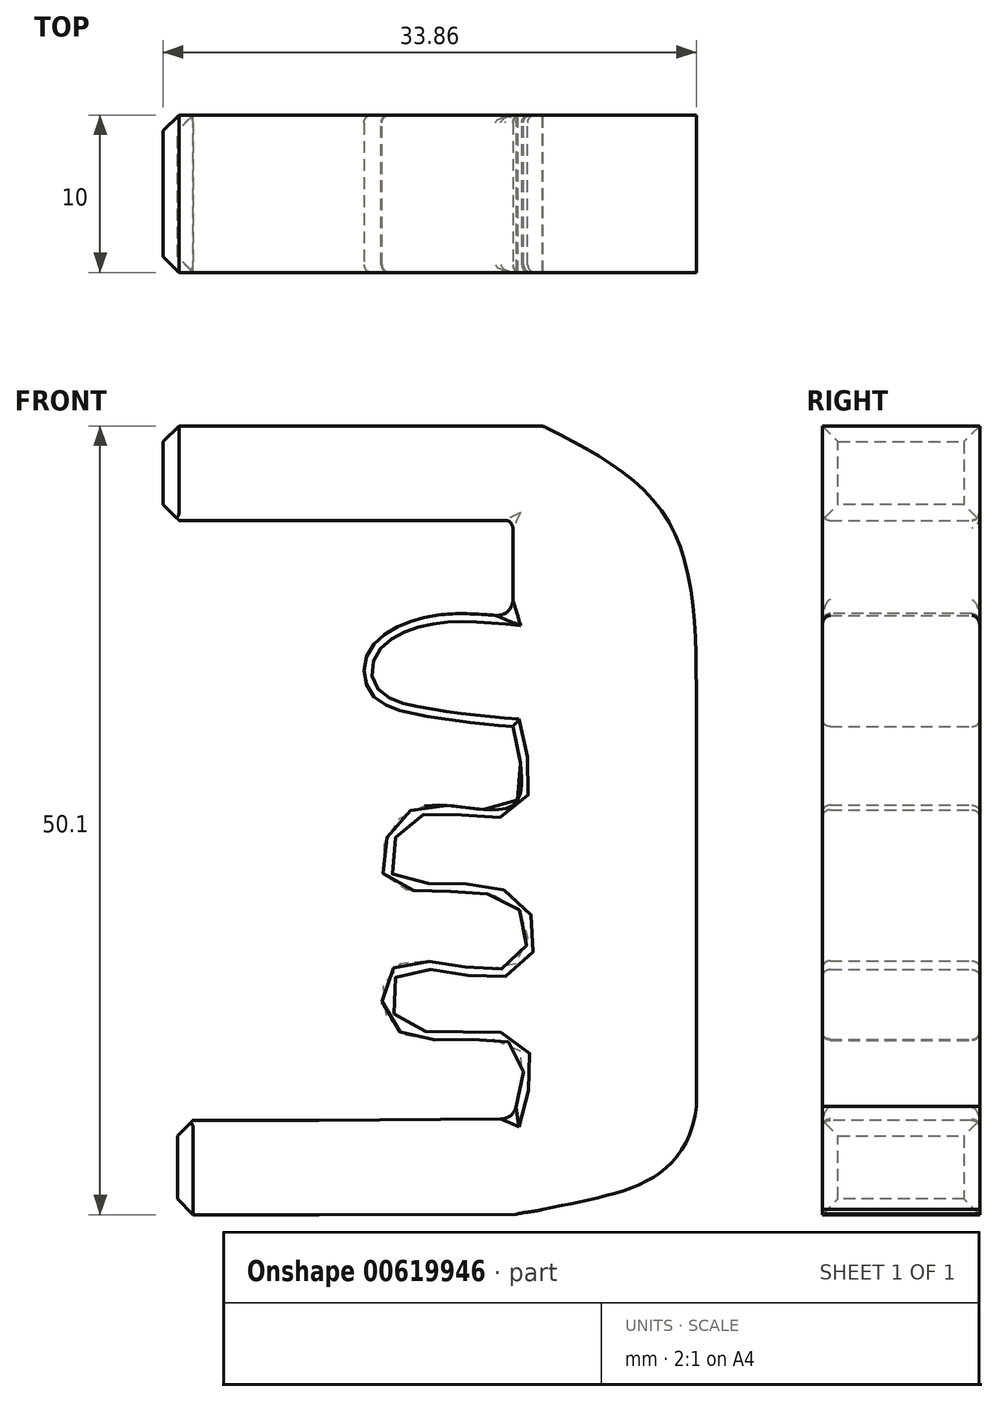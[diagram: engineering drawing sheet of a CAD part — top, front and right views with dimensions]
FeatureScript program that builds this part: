
annotation { "Feature Type Name" : "Feature", "Feature Type Description" : "" }
export const myFeature = defineFeature(function(context is Context, id is Id, definition is map)
    precondition{}
    {
        {
            var Q0;
            Q0=qCreatedBy(makeId("Front.planeOp"),FACE);
            var sketch = newSketch(context, id + "F0", { "sketchPlane" : qUnion([Q0])});
            skLineSegment(sketch, "E0.bottom", {"start": v(-57.75, 36.74) * mm, "end": v(-48.75, 36.74) * mm});
            skLineSegment(sketch, "E0.top", {"start": v(-57.75, 30.74) * mm, "end": v(-48.75, 30.74) * mm});
            skLineSegment(sketch, "E0.left", {"start": v(-57.75, 36.74) * mm, "end": v(-57.75, 30.74) * mm});
            skLineSegment(sketch, "E0.right", {"start": v(-48.75, 36.74) * mm, "end": v(-48.75, 30.74) * mm});
            skLineSegment(sketch, "E1.bottom", {"start": v(-56.85, -7.36) * mm, "end": v(-47.85, -7.36) * mm});
            skLineSegment(sketch, "E1.top", {"start": v(-56.85, -13.36) * mm, "end": v(-47.85, -13.36) * mm});
            skLineSegment(sketch, "E1.left", {"start": v(-56.85, -7.36) * mm, "end": v(-56.85, -13.36) * mm});
            skLineSegment(sketch, "E1.right", {"start": v(-47.85, -7.36) * mm, "end": v(-47.85, -13.36) * mm});
            skFitSpline(sketch, "E2", {"points": [v(-48.75, 36.74) * mm, v(-33.64, 36.74) * mm], "startDerivative": vector(17.1, 0) * mm, "endDerivative": vector(17.1, 0) * mm});
            skFitSpline(sketch, "E3", {"points": [v(-33.64, 36.74) * mm, v(-25.7, 30.74) * mm, v(-23.9, 19.03) * mm], "startDerivative": vector(20.1, -10.1) * mm, "endDerivative": vector(-0.03, -25.1) * mm});
            skFitSpline(sketch, "E4", {"points": [v(-23.9, 19.03) * mm, v(-23.89, 3) * mm], "startDerivative": vector(0, -15.9) * mm, "endDerivative": vector(0, -15.9) * mm});
            skFitSpline(sketch, "E5", {"points": [v(-23.89, 3) * mm, v(-23.89, -6.48) * mm], "startDerivative": vector(0, -10.8) * mm, "endDerivative": vector(0, -10.8) * mm});
            skFitSpline(sketch, "E6", {"points": [v(-23.89, -6.48) * mm, v(-33.64, -13.03) * mm], "startDerivative": vector(-1.93, -15.73) * mm, "endDerivative": vector(-13.6, -2.99) * mm});
            skFitSpline(sketch, "E7", {"points": [v(-48.75, 30.74) * mm, v(-35.54, 30.74) * mm], "startDerivative": vector(13.5, 0) * mm, "endDerivative": vector(13.5, 0) * mm});
            skFitSpline(sketch, "E8", {"points": [v(-35.54, 30.74) * mm, v(-35.54, 24.6) * mm], "startDerivative": vector(0, -6) * mm, "endDerivative": vector(0, -6) * mm});
            skFitSpline(sketch, "E9", {"points": [v(-35.54, 24.6) * mm, v(-41.04, 24.6) * mm, v(-44.7, 22.4) * mm, v(-44.45, 19.63) * mm, v(-40.66, 18.25) * mm, v(-35.54, 17.64) * mm], "startDerivative": vector(-25.8, 2.5) * mm, "endDerivative": vector(24.5, -1.76) * mm});
            skFitSpline(sketch, "E10", {"points": [v(-35.54, 17.64) * mm, v(-35.54, 12.64) * mm, v(-40.66, 12.64) * mm, v(-43.43, 10.86) * mm, v(-43.25, 7.65) * mm, v(-35.54, 6.4) * mm, v(-35.54, 2.48) * mm, v(-42.9, 2.48) * mm, v(-42.9, -1.63) * mm, v(-35.54, -2.52) * mm, v(-35.54, -7.28) * mm], "startDerivative": vector(15.19, -66.55) * mm, "endDerivative": vector(-18.85, -66.96) * mm});
            skLineSegment(sketch, "E11", {"start": v(-35.54, -7.28) * mm, "end": v(-47.85, -7.36) * mm});
            skFitSpline(sketch, "E12", {"points": [v(-33.64, -13.03) * mm, v(-35.28, -13.33) * mm], "startDerivative": vector(-1.5, -0.46) * mm, "endDerivative": vector(-1.5, -0.46) * mm});
            skLineSegment(sketch, "E13", {"start": v(-35.28, -13.33) * mm, "end": v(-47.85, -13.36) * mm});
            skSolve(sketch);
        }
        {
            var Q0;
            Q0 = qSketchRegion(id + "F0", true);
            extrude(context, id + "F1", {"entities" : qUnion([Q0]), "depth" : 10 * mm, "offsetDistance" : 25 * mm});
        }
        {
            var Q0;
            Q0=makeQuery(id+"F1.opExtrude","CAP_EDGE",EDGE,{"disambiguationData":[OSD([sQuery(id+"F0.wireOp",EDGE,"E0.left")])],"isStart":false});
            var Q1;
            Q1=makeQuery(id+"F1.opExtrude","CAP_EDGE",EDGE,{"disambiguationData":[OSD([sQuery(id+"F0.wireOp",EDGE,"E0.left")])],"isStart":true});
            var Q2;
            Q2=makeQuery(id+"F1.opExtrude","CAP_EDGE",EDGE,{"disambiguationData":[OSD([sQuery(id+"F0.wireOp",EDGE,"E1.left")])],"isStart":true});
            var Q3;
            Q3=makeQuery(id+"F1.opExtrude","CAP_EDGE",EDGE,{"disambiguationData":[OSD([sQuery(id+"F0.wireOp",EDGE,"E1.left")])],"isStart":false});
            var Q4;
            Q4=makeQuery(id+"F1.opExtrude","SWEPT_EDGE",EDGE,{"disambiguationData":[OSD([sQuery(id+"F0.wireOp",EDGE,"E0.bottom"),sQuery(id+"F0.wireOp",EDGE,"E0.left")])]});
            var Q5;
            Q5=makeQuery(id+"F1.opExtrude","SWEPT_EDGE",EDGE,{"disambiguationData":[OSD([sQuery(id+"F0.wireOp",EDGE,"E0.top"),sQuery(id+"F0.wireOp",EDGE,"E0.left")])]});
            var Q6;
            Q6=makeQuery(id+"F1.opExtrude","SWEPT_EDGE",EDGE,{"disambiguationData":[OSD([sQuery(id+"F0.wireOp",EDGE,"E1.bottom"),sQuery(id+"F0.wireOp",EDGE,"E1.left")])]});
            var Q7;
            Q7=makeQuery(id+"F1.opExtrude","SWEPT_EDGE",EDGE,{"disambiguationData":[OSD([sQuery(id+"F0.wireOp",EDGE,"E1.top"),sQuery(id+"F0.wireOp",EDGE,"E1.left")])]});
            chamfer(context, id + "F2", {"entities" : qUnion([Q0, Q1, Q2, Q3, Q4, Q5, Q6, Q7]), "width" : 1 * mm, "tangentPropagation" : true});
        }
        {
            var Q0;
            Q0=makeQuery(id+"F1.opExtrude","CAP_EDGE",EDGE,{"disambiguationData":[OSD([sQuery(id+"F0.wireOp",EDGE,"E0.top")])],"isStart":true});
            var Q1;
            Q1=makeQuery(id+"F1.opExtrude","CAP_EDGE",EDGE,{"disambiguationData":[OSD([sQuery(id+"F0.wireOp",EDGE,"E7")])],"isStart":true});
            var Q2;
            Q2=makeQuery(id+"F1.opExtrude","CAP_EDGE",EDGE,{"disambiguationData":[OSD([sQuery(id+"F0.wireOp",EDGE,"E8")])],"isStart":true});
            var Q3;
            Q3=makeQuery(id+"F1.opExtrude","CAP_EDGE",EDGE,{"disambiguationData":[OSD([sQuery(id+"F0.wireOp",EDGE,"E9")])],"isStart":true});
            var Q4;
            Q4=makeQuery(id+"F1.opExtrude","CAP_EDGE",EDGE,{"disambiguationData":[OSD([sQuery(id+"F0.wireOp",EDGE,"E10")])],"isStart":true});
            var Q5;
            Q5=makeQuery(id+"F1.opExtrude","CAP_EDGE",EDGE,{"disambiguationData":[OSD([sQuery(id+"F0.wireOp",EDGE,"E11")])],"isStart":true});
            var Q6;
            Q6=makeQuery(id+"F1.opExtrude","CAP_EDGE",EDGE,{"disambiguationData":[OSD([sQuery(id+"F0.wireOp",EDGE,"E1.bottom")])],"isStart":true});
            var Q7;
            Q7=qNothing();
            fillet(context, id + "F3", {"entities" : qUnion([Q0, Q1, Q2, Q3, Q4, Q5, Q6, Q7]), "radius" : 0.5 * mm, "tangentPropagation" : true, "allowEdgeOverflow" : false});
        }
        {
            var Q0;
            Q0=makeQuery(id+"F1.opExtrude","CAP_EDGE",EDGE,{"disambiguationData":[OSD([sQuery(id+"F0.wireOp",EDGE,"E7")])],"isStart":false});
            var Q1;
            Q1=makeQuery(id+"F1.opExtrude","CAP_EDGE",EDGE,{"disambiguationData":[OSD([sQuery(id+"F0.wireOp",EDGE,"E8")])],"isStart":false});
            var Q2;
            Q2=makeQuery(id+"F1.opExtrude","CAP_EDGE",EDGE,{"disambiguationData":[OSD([sQuery(id+"F0.wireOp",EDGE,"E9")])],"isStart":false});
            var Q3;
            Q3=makeQuery(id+"F1.opExtrude","CAP_EDGE",EDGE,{"disambiguationData":[OSD([sQuery(id+"F0.wireOp",EDGE,"E10")])],"isStart":false});
            var Q4;
            Q4=makeQuery(id+"F1.opExtrude","CAP_EDGE",EDGE,{"disambiguationData":[OSD([sQuery(id+"F0.wireOp",EDGE,"E10")])],"isStart":false});
            var Q5;
            Q5=makeQuery(id+"F1.opExtrude","CAP_EDGE",EDGE,{"disambiguationData":[OSD([sQuery(id+"F0.wireOp",EDGE,"E11")])],"isStart":false});
            var Q6;
            Q6=makeQuery(id+"F1.opExtrude","CAP_EDGE",EDGE,{"disambiguationData":[OSD([sQuery(id+"F0.wireOp",EDGE,"E1.bottom")])],"isStart":false});
            var Q7;
            Q7=makeQuery(id+"F1.opExtrude","SWEPT_EDGE",EDGE,{"disambiguationData":[OSD([sQuery(id+"F0.wireOp",EDGE,"E7"),sQuery(id+"F0.wireOp",EDGE,"E8")])]});
            fillet(context, id + "F4", {"entities" : qUnion([Q0, Q1, Q2, Q3, Q4, Q5, Q6, Q7]), "radius" : 0.5 * mm, "tangentPropagation" : true, "allowEdgeOverflow" : false});
        }
        {
            var Q0;
            Q0=makeQuery(id+"F1.opExtrude","SWEPT_EDGE",EDGE,{"disambiguationData":[OSD([sQuery(id+"F0.wireOp",EDGE,"E6"),sQuery(id+"F0.wireOp",EDGE,"E12")])]});
            var Q1;
            Q1=makeQuery(id+"F1.opExtrude","SWEPT_EDGE",EDGE,{"disambiguationData":[OSD([sQuery(id+"F0.wireOp",EDGE,"E12"),sQuery(id+"F0.wireOp",EDGE,"E13")])]});
            chamfer(context, id + "F5", {"entities" : qUnion([Q0, Q1]), "width" : 0.5 * mm, "tangentPropagation" : true});
        }
        {
            var Q0;
            Q0=makeQuery(id+"F1.opExtrude","SWEPT_EDGE",EDGE,{"disambiguationData":[OSD([sQuery(id+"F0.wireOp",EDGE,"E2"),sQuery(id+"F0.wireOp",EDGE,"E3")])]});
            var Q1;
            Q1=makeQuery(id+"F1.opExtrude","SWEPT_EDGE",EDGE,{"disambiguationData":[OSD([sQuery(id+"F0.wireOp",EDGE,"E10"),sQuery(id+"F0.wireOp",EDGE,"E11")])]});
            var Q2;
            Q2=makeQuery(id+"F1.opExtrude","SWEPT_EDGE",EDGE,{"disambiguationData":[OSD([sQuery(id+"F0.wireOp",EDGE,"E8"),sQuery(id+"F0.wireOp",EDGE,"E9")])]});
            fillet(context, id + "F6", {"entities" : qUnion([Q0, Q1, Q2]), "radius" : 1 * mm, "tangentPropagation" : true, "allowEdgeOverflow" : false});
        }
    });
